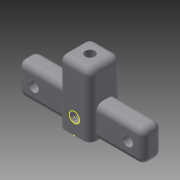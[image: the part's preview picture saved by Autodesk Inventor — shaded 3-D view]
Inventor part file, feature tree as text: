
AUTODESK INVENTOR PART (.ipt)
format: ipt  version: 2015 (Build 190159000, 159)  size: 200,192 bytes
history: native  units: mm
features: sketch x6, hole x3, fillet x3, extrude x2, plane x2, mirror x1
ambient origin geometry x8: Origin, YZ Plane, XZ Plane, XY Plane, X Axis, Y Axis, Z Axis, Center Point
bodies: Body1 (feature_tree)
feature tree (17):
  extrude  "Extrusion3"  Depth=10.0mm
  hole  "Hole4"  [1 undecoded]
  hole  "Hole5"  [1 undecoded]
  extrude  "Extrusion4"  Depth=6.0mm
  plane  "Work Plane2"
  plane  "Work Plane1"
  mirror  "Mirror1"
  fillet  "Fillet3"  Radius=15.0mm
  fillet  "Fillet4"  Radius=2.0mm
  fillet  "Fillet5"  Radius=2.0mm
  sketch  "Sketch11"  dims[d45=3.3mm d46=6.0mm d47=4.1mm d48=5.0mm d49=90.0deg d50=8.0mm d51=0.0mm d52=6.0mm d53=15.0mm d54=0.0mm d64=2.0mm d65=2.0mm]
  hole  "Hole7"  [1 undecoded]
  sketch  "Sketch6"  dims[d31=10.0mm d32=10.0mm]
  sketch  "Sketch7"  dims[d33=5.0mm d34=5.0mm]
  sketch  "Sketch8"  dims[d35=20.0mm d36=0.0mm]
  sketch  "Sketch9"  dims[d37=3.1mm d38=6.0mm d39=4.0mm d40=2.0mm d41=90.0deg d42=8.0mm d43=0.0mm d44=5.0mm]
  sketch  "Sketch12"  dims[d66=2.0mm d67=5.0mm d68=5.0mm d69=3.3mm d70=6.0mm d71=4.1mm d72=4.0mm d73=90.0deg d74=8.0mm d75=20.594885mm]
note: 3 required parameter values undecoded (feature->parameter linkage not recoverable at this tier; creation-order binding heuristic only, values carry confidence <= 0.55)
